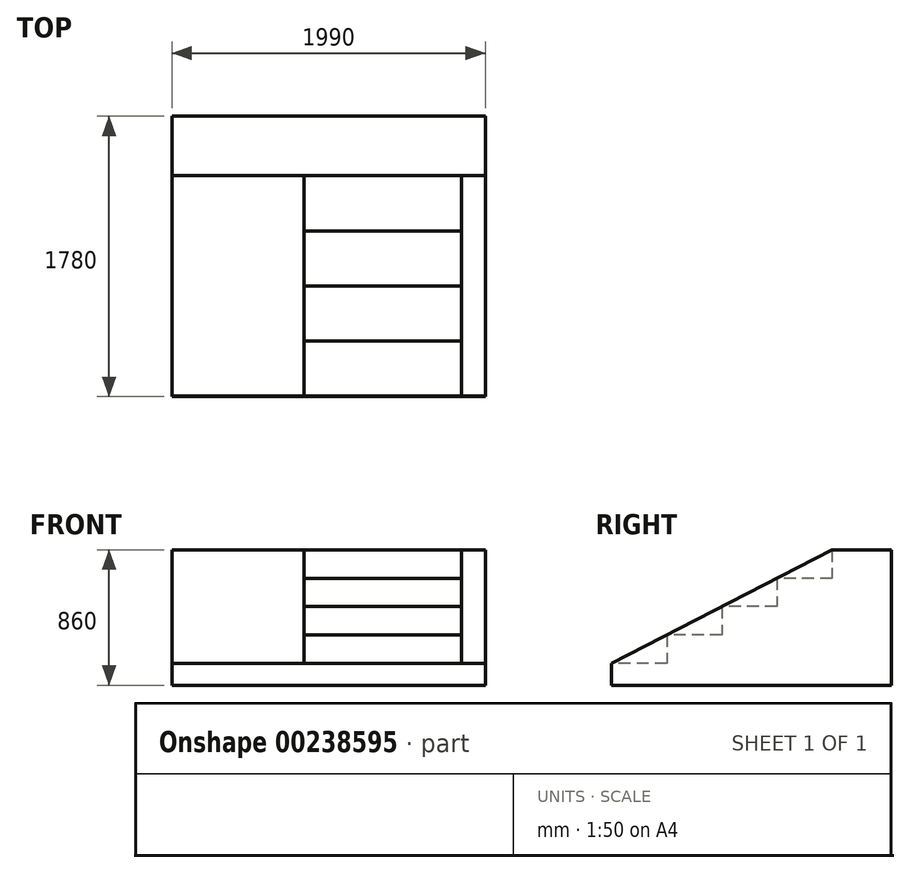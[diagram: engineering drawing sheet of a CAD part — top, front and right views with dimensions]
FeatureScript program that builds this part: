
annotation { "Feature Type Name" : "Feature", "Feature Type Description" : "" }
export const myFeature = defineFeature(function(context is Context, id is Id, definition is map)
    precondition{}
    {
        {
            var Q0;
            Q0=qCreatedBy(makeId("Right.planeOp"),FACE);
            var sketch = newSketch(context, id + "F0", { "sketchPlane" : qUnion([Q0])});
            skLineSegment(sketch, "E0", {"start": v(0, 0) * mm, "end": v(-1780, 0) * mm});
            skLineSegment(sketch, "E1", {"start": v(0, 0) * mm, "end": v(0, 860) * mm});
            skLineSegment(sketch, "E2", {"start": v(0, 860) * mm, "end": v(-377.9, 860) * mm});
            skLineSegment(sketch, "E3", {"start": v(-377.9, 860) * mm, "end": v(-377.9, 679.98) * mm});
            skLineSegment(sketch, "E4", {"start": v(-377.9, 679.98) * mm, "end": v(-727.9, 679.98) * mm});
            skLineSegment(sketch, "E5", {"start": v(-727.9, 679.98) * mm, "end": v(-727.9, 499.98) * mm});
            skLineSegment(sketch, "E6", {"start": v(-727.9, 499.98) * mm, "end": v(-1077.9, 499.98) * mm});
            skLineSegment(sketch, "E7", {"start": v(-1077.9, 499.98) * mm, "end": v(-1077.9, 319.98) * mm});
            skLineSegment(sketch, "E8", {"start": v(-1077.9, 319.98) * mm, "end": v(-1427.9, 319.98) * mm});
            skLineSegment(sketch, "E9", {"start": v(-1427.9, 319.98) * mm, "end": v(-1427.9, 139.98) * mm});
            skLineSegment(sketch, "E10", {"start": v(-1427.9, 139.98) * mm, "end": v(-1777.9, 139.98) * mm});
            skLineSegment(sketch, "E11", {"start": v(-1777.9, 139.98) * mm, "end": v(-1780, 0) * mm});
            skSolve(sketch);
        }
        {
            var Q0;
            Q0 = qSketchRegion(id + "F0", true);
            extrude(context, id + "F1", {"entities" : qUnion([Q0]), "depth" : 500 * mm, "hasSecondDirection" : true, "secondDirectionOppositeDirection" : true, "secondDirectionDepth" : 500 * mm});
        }
        {
            var Q0;
            Q0=makeQuery(id+"F1.opExtrude","CAP_FACE",FACE,{"disambiguationData":[OSD([sQuery(id+"F0.wireOp",EDGE,"E0"),sQuery(id+"F0.wireOp",EDGE,"E1"),sQuery(id+"F0.wireOp",EDGE,"E2"),sQuery(id+"F0.wireOp",EDGE,"E3"),sQuery(id+"F0.wireOp",EDGE,"E4"),sQuery(id+"F0.wireOp",EDGE,"E5"),sQuery(id+"F0.wireOp",EDGE,"E6"),sQuery(id+"F0.wireOp",EDGE,"E7"),sQuery(id+"F0.wireOp",EDGE,"E8"),sQuery(id+"F0.wireOp",EDGE,"E9"),sQuery(id+"F0.wireOp",EDGE,"E10"),sQuery(id+"F0.wireOp",EDGE,"E11")])],"isStart":false});
            var sketch = newSketch(context, id + "F2", { "sketchPlane" : qUnion([Q0])});
            skLineSegment(sketch, "E12", {"start": v(-377.9, 860) * mm, "end": v(0, 860) * mm});
            skLineSegment(sketch, "E13", {"start": v(0, 860) * mm, "end": v(0, 0) * mm});
            skLineSegment(sketch, "E14", {"start": v(0, 0) * mm, "end": v(-1780, 0) * mm});
            skLineSegment(sketch, "E15", {"start": v(-1780, 0) * mm, "end": v(-1777.9, 139.98) * mm});
            skLineSegment(sketch, "E16", {"start": v(-1777.9, 139.98) * mm, "end": v(-377.9, 860) * mm});
            skSolve(sketch);
        }
        {
            var Q0;
            Q0 = qSketchRegion(id + "F2", true);
            extrude(context, id + "F3", {"entities" : qUnion([Q0]), "operationType" : NewBodyOperationType.ADD, "depth" : 150 * mm});
        }
        {
            var Q0;
            Q0=makeQuery(id+"F1.opExtrude","CAP_FACE",FACE,{"disambiguationData":[OSD([sQuery(id+"F0.wireOp",EDGE,"E0"),sQuery(id+"F0.wireOp",EDGE,"E1"),sQuery(id+"F0.wireOp",EDGE,"E2"),sQuery(id+"F0.wireOp",EDGE,"E3"),sQuery(id+"F0.wireOp",EDGE,"E4"),sQuery(id+"F0.wireOp",EDGE,"E5"),sQuery(id+"F0.wireOp",EDGE,"E6"),sQuery(id+"F0.wireOp",EDGE,"E7"),sQuery(id+"F0.wireOp",EDGE,"E8"),sQuery(id+"F0.wireOp",EDGE,"E9"),sQuery(id+"F0.wireOp",EDGE,"E10"),sQuery(id+"F0.wireOp",EDGE,"E11")])],"isStart":true});
            var sketch = newSketch(context, id + "F4", { "sketchPlane" : qUnion([Q0])});
            skLineSegment(sketch, "E17", {"start": v(1777.9, 139.98) * mm, "end": v(1780, 0) * mm});
            skLineSegment(sketch, "E18", {"start": v(1780, 0) * mm, "end": v(0, 0) * mm});
            skLineSegment(sketch, "E19", {"start": v(0, 0) * mm, "end": v(0, 860) * mm});
            skLineSegment(sketch, "E20", {"start": v(0, 860) * mm, "end": v(377.9, 860) * mm});
            skLineSegment(sketch, "E21", {"start": v(377.9, 860) * mm, "end": v(1777.9, 139.98) * mm});
            skSolve(sketch);
        }
        {
            var Q0;
            Q0 = qSketchRegion(id + "F4", true);
            extrude(context, id + "F5", {"entities" : qUnion([Q0]), "operationType" : NewBodyOperationType.ADD, "depth" : 840 * mm});
        }
    });
